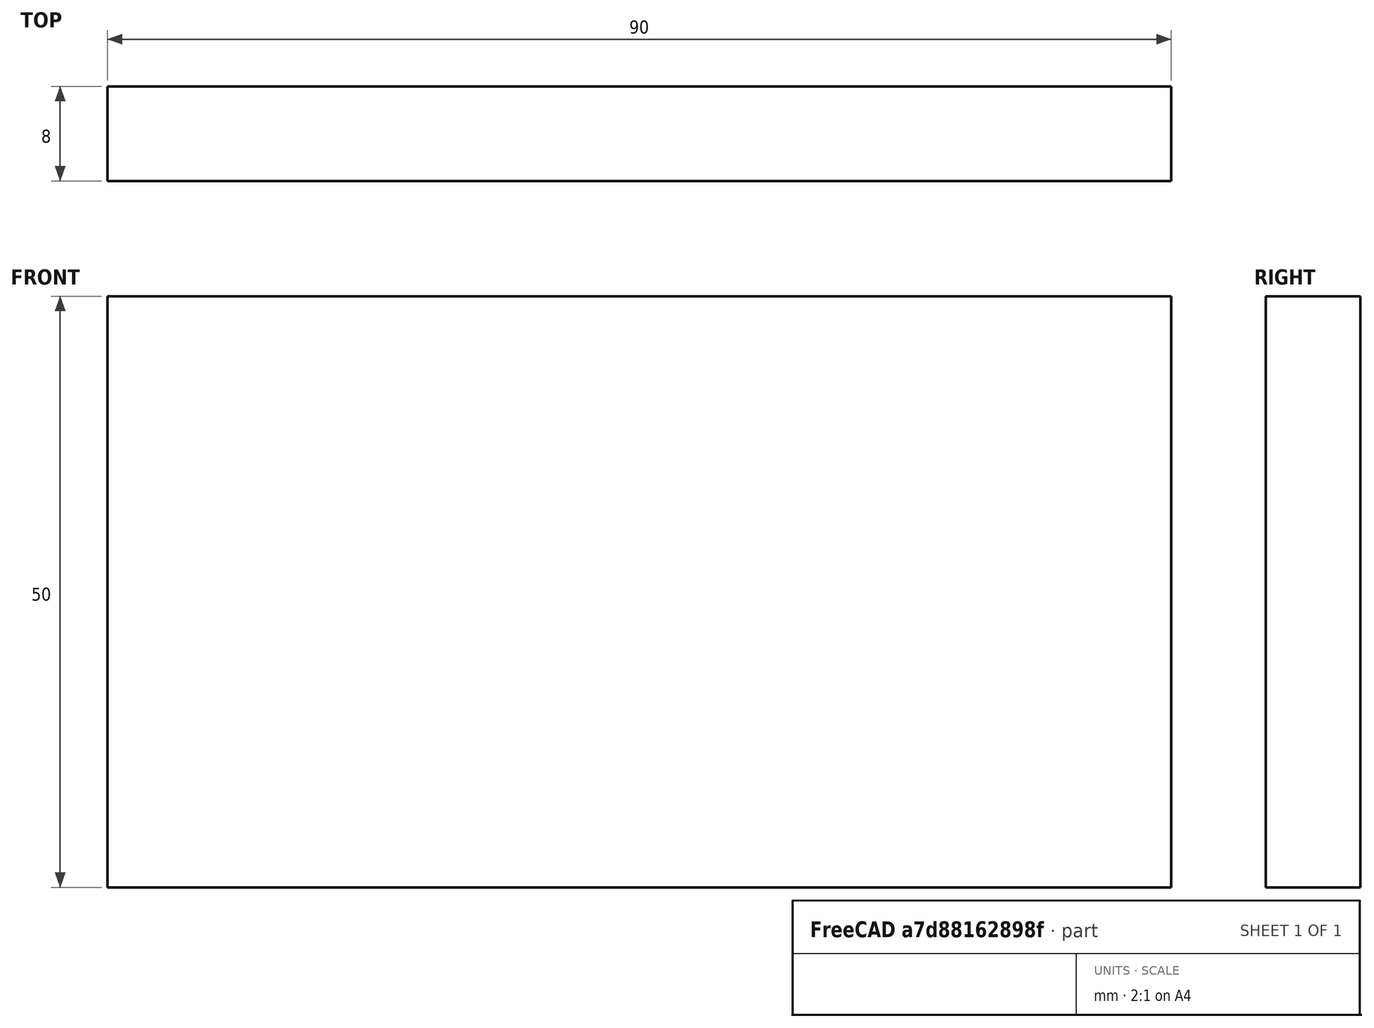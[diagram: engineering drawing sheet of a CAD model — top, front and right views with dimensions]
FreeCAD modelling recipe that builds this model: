
FCSTD DOCUMENT  (FreeCAD 0.15R4671 (Git))
Label: Flat Bar 90x8 EN10058 S235JR
License: All rights reserved
LicenseURL: http://en.wikipedia.org/wiki/All_rights_reserved
objects: Sketcher::SketchObject×1, Part::Extrusion×1
note: 2 computed .brp shape members not serialized (recipe doc carries the construction recipe); baked Part::Feature solids carry a one-line shape summary decoded from their .brp

FEATURE [Sketcher::SketchObject] Sketch
  sketch-geometry (4):
    g0: LineSegment StartX=-45 StartY=-4 StartZ=0 EndX=45 EndY=-4 EndZ=0
    g1: LineSegment StartX=45 StartY=-4 StartZ=0 EndX=45 EndY=4 EndZ=0
    g2: LineSegment StartX=45 StartY=4 StartZ=0 EndX=-45 EndY=4 EndZ=0
    g3: LineSegment StartX=-45 StartY=4 StartZ=0 EndX=-45 EndY=-4 EndZ=0
  constraints (12):
    c: Coincident(g0,g1)
    c: Coincident(g1,g2)
    c: Coincident(g2,g3)
    c: Coincident(g3,g0)
    c: Horizontal(g0)
    c: Horizontal(g2)
    c: Vertical(g1)
    c: Vertical(g3)
    c: Symmetric(g1,g2,g-2)
    c: Symmetric(g0,g1,g-1)
    c: DistanceY(g1) = 8
    c: DistanceX(g0) = 90
FEATURE [Part::Extrusion] Extrude  label="Flat Bar 90x8 EN10058 S235JR"
  Base = -> Sketch
  Dir = (0,0,50)
  Solid = true
